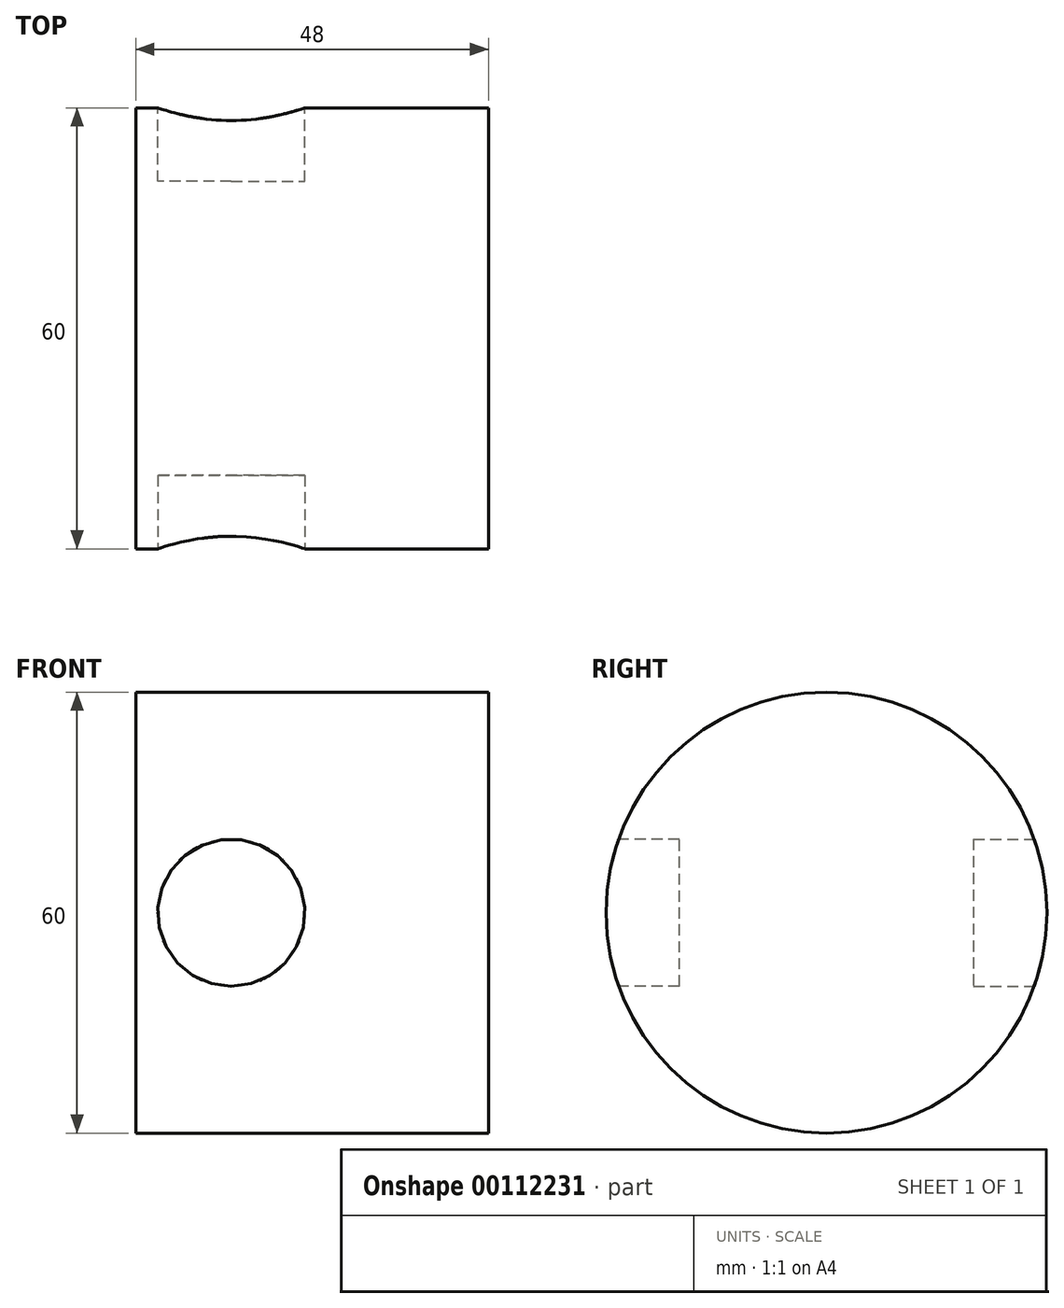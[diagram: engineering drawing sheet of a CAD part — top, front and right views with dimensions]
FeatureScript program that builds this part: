
annotation { "Feature Type Name" : "Feature", "Feature Type Description" : "" }
export const myFeature = defineFeature(function(context is Context, id is Id, definition is map)
    precondition{}
    {
        {
            var Q0;
            Q0=qCreatedBy(makeId("Right.planeOp"),FACE);
            var sketch = newSketch(context, id + "F0", { "sketchPlane" : qUnion([Q0])});
            skCircle(sketch, "E0", {"center": v(0, 0) * mm, "radius": 30 * mm});
            skSolve(sketch);
        }
        {
            var Q0;
            Q0=makeQuery(id+"F0.imprint","IMPRINT",FACE,{"disambiguationData":[TD([[makeQuery(id+"F0.imprint","IMPRINT",EDGE,{"derivedFrom":sQuery(id+"F0.wireOp",EDGE,"E0")}),1.0]])]});
            extrude(context, id + "F1", {"entities" : qUnion([Q0]), "depth" : 48 * mm});
        }
        {
            var Q0;
            Q0=qCreatedBy(makeId("Front.planeOp"),FACE);
            cPlane(context, id + "F2", {"entities" : qUnion([Q0]), "cplaneType" : CPlaneType.OFFSET, "offset" : 30 * mm, "width" : 150 * mm, "height" : 150 * mm});
        }
        {
            var Q0;
            Q0=qCreatedBy(id+"F2.planeOp",FACE);
            var sketch = newSketch(context, id + "F3", { "sketchPlane" : qUnion([Q0])});
            skCircle(sketch, "E1", {"center": v(13, 0) * mm, "radius": 10 * mm});
            skSolve(sketch);
        }
        {
            var Q0;
            Q0=makeQuery(id+"F3.imprint","IMPRINT",FACE,{"disambiguationData":[TD([[makeQuery(id+"F3.imprint","IMPRINT",EDGE,{"derivedFrom":sQuery(id+"F3.wireOp",EDGE,"E1")}),1.0]])]});
            extrude(context, id + "F4", {"entities" : qUnion([Q0]), "operationType" : NewBodyOperationType.REMOVE, "oppositeDirection" : true, "depth" : 10 * mm});
        }
        {
            var Q0;
            Q0=qCreatedBy(makeId("Front.planeOp"),FACE);
            cPlane(context, id + "F5", {"entities" : qUnion([Q0]), "cplaneType" : CPlaneType.OFFSET, "offset" : 30 * mm, "oppositeDirection" : true, "width" : 150 * mm, "height" : 150 * mm});
        }
        {
            var Q0;
            Q0=qCreatedBy(id+"F5.planeOp",FACE);
            var sketch = newSketch(context, id + "F6", { "sketchPlane" : qUnion([Q0])});
            skCircle(sketch, "E2", {"center": v(13, 0) * mm, "radius": 10 * mm});
            skSolve(sketch);
        }
        {
            var Q0;
            Q0=makeQuery(id+"F6.imprint","IMPRINT",FACE,{"disambiguationData":[TD([[makeQuery(id+"F6.imprint","IMPRINT",EDGE,{"derivedFrom":sQuery(id+"F6.wireOp",EDGE,"E2")}),1.0]])]});
            extrude(context, id + "F7", {"entities" : qUnion([Q0]), "operationType" : NewBodyOperationType.REMOVE, "depth" : 10 * mm});
        }
    });
